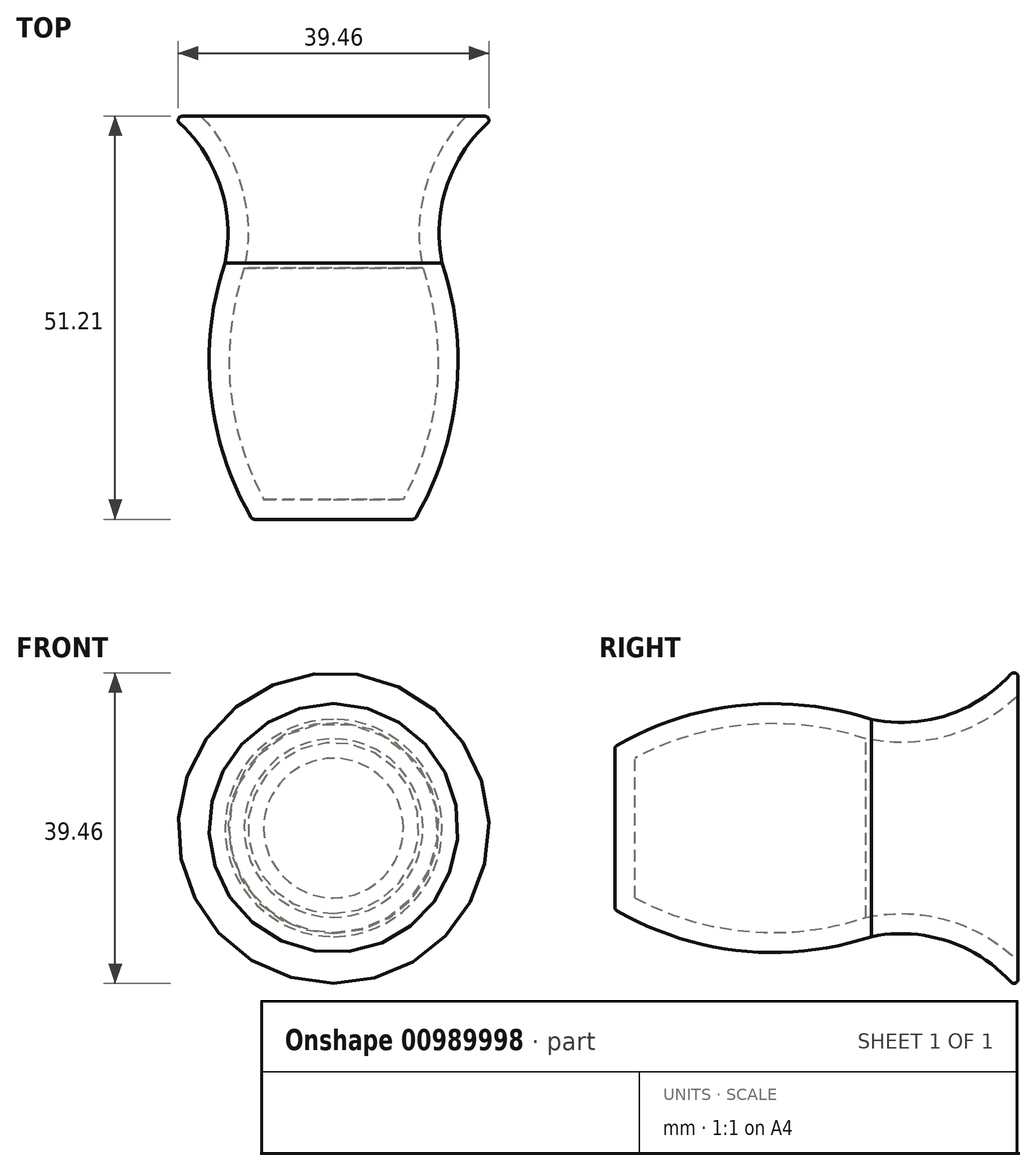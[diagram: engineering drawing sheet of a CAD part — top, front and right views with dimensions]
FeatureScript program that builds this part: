
annotation { "Feature Type Name" : "Feature", "Feature Type Description" : "" }
export const myFeature = defineFeature(function(context is Context, id is Id, definition is map)
    precondition{}
    {
        {
            var Q0;
            Q0=qCreatedBy(makeId("Top.planeOp"),FACE);
            var sketch = newSketch(context, id + "F0", { "sketchPlane" : qUnion([Q0])});
            skLineSegment(sketch, "E0", {"start": v(0, 0) * mm, "end": v(10.35, 0) * mm});
            skArc(sketch, "E1", {"start": v(10.35, 0) * mm, "mid": v(15.58, 15.91) * mm, "end": v(13.8, 32.57) * mm});
            skArc(sketch, "E2", {"start": v(20.61, 51.2) * mm, "mid": v(14.56, 42.85) * mm, "end": v(13.8, 32.57) * mm});
            skLineSegment(sketch, "E3", {"start": v(20.61, 51.2) * mm, "end": v(0, 51.2) * mm});
            skLineSegment(sketch, "E4", {"start": v(0, 0) * mm, "end": v(0, 51.2) * mm});
            skSolve(sketch);
        }
        {
            var Q0;
            Q0=makeQuery(id+"F0.imprint","IMPRINT",FACE,{"disambiguationData":[TD([[makeQuery(id+"F0.imprint","IMPRINT",EDGE,{"derivedFrom":sQuery(id+"F0.wireOp",EDGE,"E0")}),1.0]])]});
            var Q1;
            Q1=sQuery(id+"F0.wireOp",EDGE,"E4");
            revolve(context, id + "F1", {"surfaceOperationType" : NewSurfaceOperationType.NEW, "entities" : qUnion([Q0]), "axis" : qUnion([Q1]), "revolveType" : RevolveType.FULL});
        }
        {
            var Q0;
            Q0=makeQuery(id+"F1.opRevolve","SWEPT_FACE",FACE,{"disambiguationData":[OSD([sQuery(id+"F0.wireOp",EDGE,"E3")])]});
            shell(context, id + "F2", {"entities" : qUnion([Q0]), "thickness" : 2.54 * mm});
        }
        {
            var Q0;
            Q0=makeQuery(id+"F1.opRevolve","SWEPT_EDGE",EDGE,{"disambiguationData":[OSD([sQuery(id+"F0.wireOp",EDGE,"E2"),sQuery(id+"F0.wireOp",EDGE,"E3")])]});
            var Q1;
            Q1=makeQuery(id+"F2.opShell","OFFSET_EDGE",EDGE,{"disambiguationData":[OSD([sQuery(id+"F0.wireOp",EDGE,"E2"),sQuery(id+"F0.wireOp",EDGE,"E3")])]});
            var Q2;
            Q2=makeQuery(id+"F1.opRevolve","SWEPT_EDGE",EDGE,{"disambiguationData":[OSD([sQuery(id+"F0.wireOp",EDGE,"E0"),sQuery(id+"F0.wireOp",EDGE,"E1")])]});
            fillet(context, id + "F3", {"entities" : qUnion([Q0, Q1, Q2]), "radius" : 0.5 * mm, "tangentPropagation" : true, "allowEdgeOverflow" : false});
        }
    });
